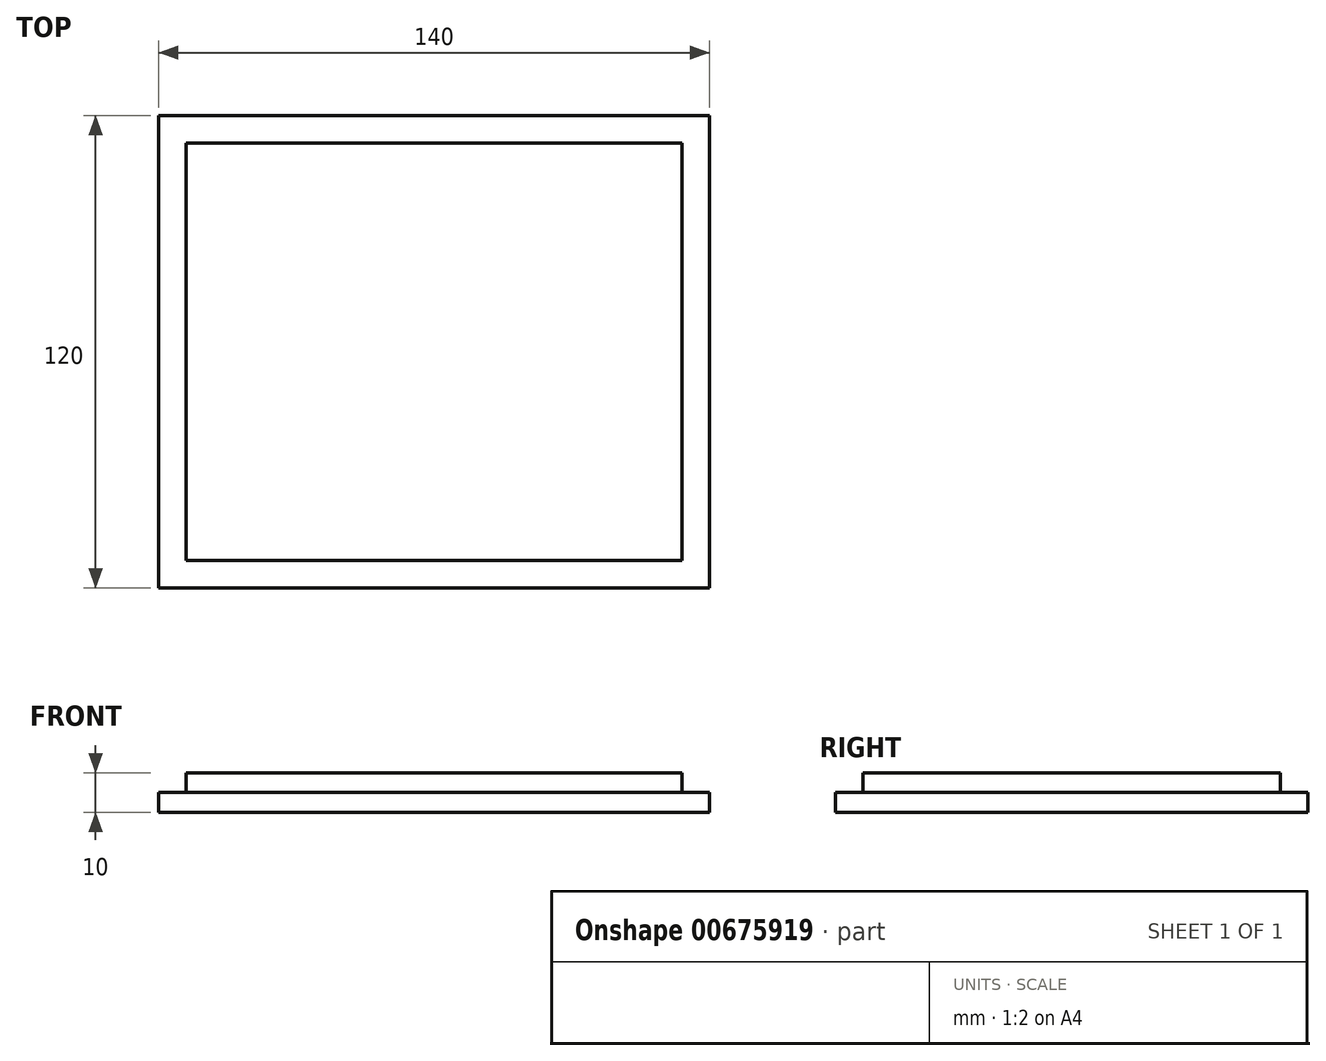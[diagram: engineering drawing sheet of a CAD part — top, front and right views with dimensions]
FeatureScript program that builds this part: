
annotation { "Feature Type Name" : "Feature", "Feature Type Description" : "" }
export const myFeature = defineFeature(function(context is Context, id is Id, definition is map)
    precondition{}
    {
        {
            var Q0;
            Q0=qCreatedBy(makeId("Top.planeOp"),FACE);
            var sketch = newSketch(context, id + "F0", { "sketchPlane" : qUnion([Q0])});
            skLineSegment(sketch, "E0.bottom", {"start": v(0, 0) * mm, "end": v(-140, 0) * mm});
            skLineSegment(sketch, "E0.top", {"start": v(0, 120) * mm, "end": v(-140, 120) * mm});
            skLineSegment(sketch, "E0.left", {"start": v(0, 0) * mm, "end": v(0, 120) * mm});
            skLineSegment(sketch, "E0.right", {"start": v(-140, 0) * mm, "end": v(-140, 120) * mm});
            skSolve(sketch);
        }
        {
            var Q0;
            Q0 = qSketchRegion(id + "F0", true);
            extrude(context, id + "F1", {"entities" : qUnion([Q0]), "depth" : 5 * mm, "offsetDistance" : 25 * mm});
        }
        {
            var Q0;
            Q0=makeQuery(id+"F1.opExtrude","CAP_FACE",FACE,{"disambiguationData":[OSD([sQuery(id+"F0.wireOp",EDGE,"E0.bottom"),sQuery(id+"F0.wireOp",EDGE,"E0.top"),sQuery(id+"F0.wireOp",EDGE,"E0.left"),sQuery(id+"F0.wireOp",EDGE,"E0.right")])],"isStart":false});
            var sketch = newSketch(context, id + "F2", { "sketchPlane" : qUnion([Q0])});
            skLineSegment(sketch, "E1.bottom", {"start": v(-140, 120) * mm, "end": v(0, 120) * mm});
            skLineSegment(sketch, "E1.top", {"start": v(-140, 0) * mm, "end": v(0, 0) * mm});
            skLineSegment(sketch, "E1.left", {"start": v(-140, 120) * mm, "end": v(-140, 0) * mm});
            skLineSegment(sketch, "E1.right", {"start": v(0, 120) * mm, "end": v(0, 0) * mm});
            skLineSegment(sketch, "E2.0", {"start": v(-133, 113) * mm, "end": v(-7, 113) * mm});
            skLineSegment(sketch, "E2.1", {"start": v(-133, 113) * mm, "end": v(-133, 7) * mm});
            skLineSegment(sketch, "E2.2", {"start": v(-133, 7) * mm, "end": v(-7, 7) * mm});
            skLineSegment(sketch, "E2.3", {"start": v(-7, 113) * mm, "end": v(-7, 7) * mm});
            skSolve(sketch);
        }
        {
            var Q0;
            Q0=makeQuery(id+"F2.imprint","IMPRINT",FACE,{"disambiguationData":[TD([[makeQuery(id+"F2.imprint","IMPRINT",EDGE,{"derivedFrom":sQuery(id+"F2.wireOp",EDGE,"E2.0")}),-1.0]])]});
            extrude(context, id + "F3", {"entities" : qUnion([Q0]), "operationType" : NewBodyOperationType.ADD, "depth" : 5 * mm, "offsetDistance" : 25 * mm});
        }
    });
